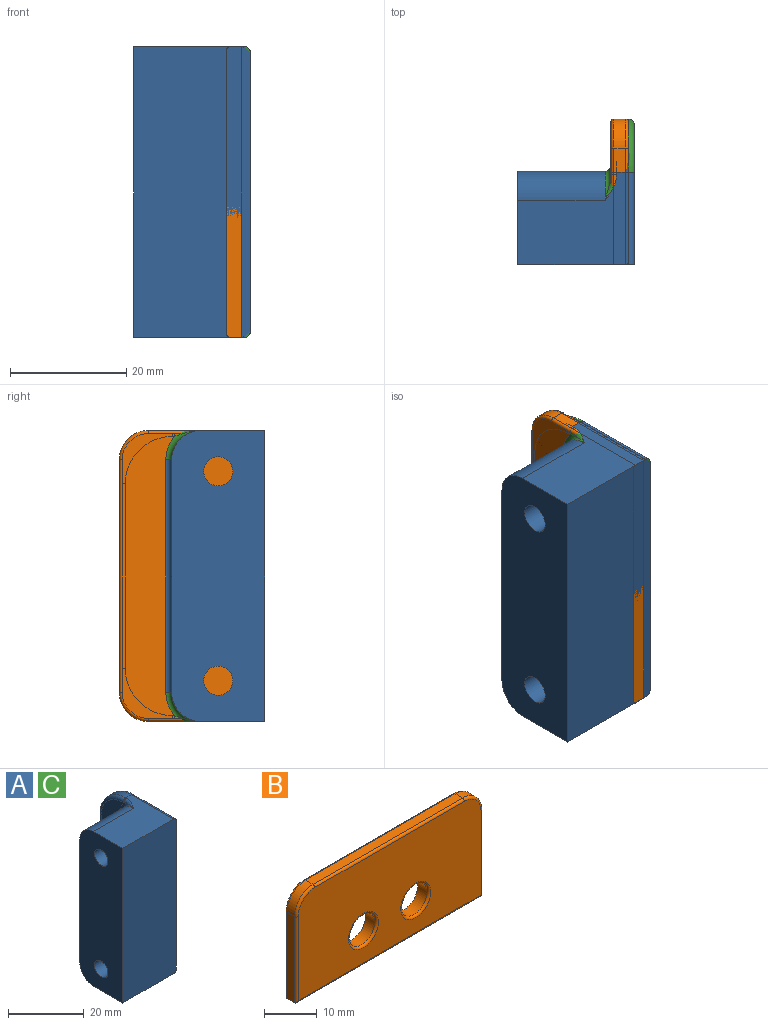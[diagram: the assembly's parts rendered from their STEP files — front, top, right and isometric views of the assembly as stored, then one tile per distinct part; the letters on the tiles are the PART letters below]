
ASSEMBLY  parts=3 mates=1
PART A: 33 faces, bbox 20x25.8x54.5 mm
  f0: cylinder r=2.5mm len=19mm, axis (1,0,0), area 298.5mm2, adj f4,f30
  f1: cylinder r=2.5mm len=19mm, axis (1,0,0), area 298.5mm2, adj f4,f32
  f2: plane 50x20mm, normal (0,-1,0), area 999.6mm2, adj f4,f5,f6,f9,f14,f16
  f3: plane 40x15mm, normal (0,1,0), area 600mm2, adj f4,f7,f8,f21
  f4: plane 50x16mm, normal (-1,0,0), area 750mm2, adj f0,f1,f2,f3,f5,f6,f7,f8
  f5: plane 19x15.83mm, normal (0,0,1), area 221.9mm2, adj f2,f4,f8,f13,f14,f20,f22
  f6: plane 19x15.83mm, normal (0,0,-1), area 221.9mm2, adj f2,f4,f7,f12,f16,f25,f27
  f7: cylinder r=5mm len=15mm, axis (-1,0,0), area 117.8mm2, adj f3,f4,f6,f23
  f8: cylinder r=5mm len=15mm, axis (1,0,0), area 117.8mm2, adj f3,f4,f5,f19
  f9: plane 48x24mm, normal (1,0,0), area 966.2mm2, adj f2,f14,f15,f16,f17,f18,f29,f31
  f10: plane 48x8.53mm, normal (-1,0,0), area 311.2mm2, adj f19,f21,f22,f23,f24,f26,f27,f28
  f11: plane 31.65x2mm, normal (0,1,0), area 63.3mm2, adj f12,f13,f17,f26
  f12: cylinder r=9.17mm len=9.17mm, axis (1,0,0), area 28.8mm2, adj f6,f11,f18,f28
  f13: cylinder r=9.17mm len=9.17mm, axis (-1,0,0), area 28.8mm2, adj f5,f11,f15,f24
  f14: cylinder r=1mm len=15.83mm, axis (0,1,0), area 24.9mm2, adj f2,f5,f9,f15
  f15: torus R=8.17mm, axis (1,0,0), area 21.7mm2, adj f9,f13,f14,f17
  f16: cylinder r=1mm len=15.83mm, axis (0,-1,0), area 24.9mm2, adj f2,f6,f9,f18
  f17: cylinder r=1mm len=31.65mm, axis (0,0,-1), area 49.7mm2, adj f9,f11,f15,f18
  f18: torus R=8.17mm, axis (1,0,0), area 21.7mm2, adj f9,f12,f16,f17
  f19: torus R=6mm, axis (1,0,0), area 9.1mm2, adj f8,f10,f20,f21
  f20: bspline ~4.47x2mm, area 3.8mm2, adj f5,f19,f22
  f21: cylinder r=1mm len=40mm, axis (0,0,1), area 62.8mm2, adj f3,f10,f19,f23
  f22: cylinder r=1mm len=1mm, axis (0,-1,0), area 0.6mm2, adj f5,f10,f20,f24
  f23: torus R=6mm, axis (1,0,0), area 9.1mm2, adj f7,f10,f21,f25
  f24: torus R=8.17mm, axis (1,0,0), area 21.7mm2, adj f10,f13,f22,f26
  f25: bspline ~4.47x2mm, area 3.8mm2, adj f6,f23,f27
  f26: cylinder r=1mm len=31.65mm, axis (0,0,1), area 49.7mm2, adj f10,f11,f24,f28
  f27: cylinder r=1mm len=1mm, axis (0,1,0), area 0.6mm2, adj f6,f10,f25,f28
  f28: torus R=8.17mm, axis (1,0,0), area 21.7mm2, adj f10,f12,f26,f27
  f29: cylinder r=5mm len=10mm, axis (1,0,0), area 31.4mm2, adj f9,f30
  f30: plane 10x10mm, normal (1,0,0), area 58.9mm2, adj f0,f29
  f31: cylinder r=5mm len=10mm, axis (1,0,0), area 31.4mm2, adj f9,f32
  f32: plane 10x10mm, normal (1,0,0), area 58.9mm2, adj f1,f31
PART B: 23 faces, bbox 50.8x3x25.4 mm
  f0: plane 20x2mm, normal (1,0,0), area 40mm2, adj f3,f8,f13,f22
  f1: plane 40x2mm, normal (0,0,1), area 80mm2, adj f8,f9,f14,f20
  f2: plane 20x2mm, normal (-1,0,0), area 40mm2, adj f3,f9,f10,f18
  f3: plane 50x2.5mm, normal (0,0,-1), area 124.9mm2, adj f0,f2,f5,f11,f18,f22
  f4: plane 49x24mm, normal (0,-1,0), area 1066.8mm2, adj f10,f11,f12,f13,f14,f15,f16,f17
  f5: plane 49x24.5mm, normal (0,1,0), area 1114.8mm2, adj f3,f6,f7,f18,f19,f20,f21,f22
  f6: cylinder r=3.5mm len=7mm, axis (0,-1,0), area 55mm2, adj f5,f16
  f7: cylinder r=3.5mm len=7mm, axis (0,-1,0), area 55mm2, adj f5,f17
  f8: cylinder r=5mm len=5mm, axis (0,1,0), area 15.7mm2, adj f0,f1,f15,f21
  f9: cylinder r=5mm len=5mm, axis (0,-1,0), area 15.7mm2, adj f1,f2,f12,f19
  f10: cylinder r=0.5mm len=20mm, axis (0,0,1), area 15.6mm2, adj f2,f4,f11,f12
  f11: cylinder r=0.5mm len=50mm, axis (-1,0,0), area 39mm2, adj f3,f4,f10,f13
  f12: torus R=4.5mm, axis (0,-1,0), area 5.9mm2, adj f4,f9,f10,f14
  f13: cylinder r=0.5mm len=20mm, axis (0,0,-1), area 15.6mm2, adj f0,f4,f11,f15
  f14: cylinder r=0.5mm len=40mm, axis (1,0,0), area 31.4mm2, adj f1,f4,f12,f15
  f15: torus R=4.5mm, axis (0,-1,0), area 5.9mm2, adj f4,f8,f13,f14
  f16: torus R=4mm, axis (0,-1,0), area 18.2mm2, adj f4,f6
  f17: torus R=4mm, axis (0,-1,0), area 18.2mm2, adj f4,f7
  f18: cylinder r=0.5mm len=20mm, axis (0,0,-1), area 15.7mm2, adj f2,f3,f5,f19
  f19: torus R=4.5mm, axis (0,-1,0), area 5.9mm2, adj f5,f9,f18,f20
  f20: cylinder r=0.5mm len=40mm, axis (-1,0,0), area 31.4mm2, adj f1,f5,f19,f21
  f21: torus R=4.5mm, axis (0,-1,0), area 5.9mm2, adj f5,f8,f20,f22
  f22: cylinder r=0.5mm len=20mm, axis (0,0,1), area 15.7mm2, adj f0,f3,f5,f21
PART C: same geometry as A
PLACE A t=(-18.88,1.3,-6.71)mm
PLACE B rot(axis=(-0.58,0.58,0.58),120deg) t=(-10.88,5.8,18.29)mm
PLACE C t=(-18.88,1.3,-6.71)mm fixed
MATE planar C.f2 <-> B.f3  axis (0,-1,0) through (-16.88,-6.7,18.29)mm
